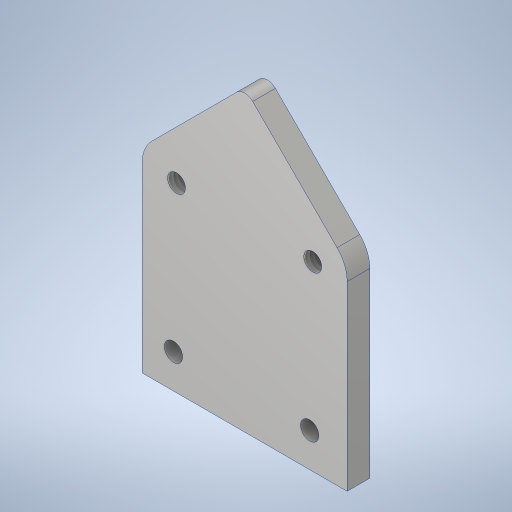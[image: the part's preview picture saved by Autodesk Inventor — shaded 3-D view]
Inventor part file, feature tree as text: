
AUTODESK INVENTOR PART (.ipt)
format: ipt  version: 2023.4 (Build 274418000, 418)  size: 270,848 bytes
history: native  units: in
note: dims shown in document units (in); Inventor stores cm internally (conversion verified against a paired STEP export)
features: sketch x2, hole x2, extrude x1
ambient origin geometry x8: Origin, YZ Plane, XZ Plane, XY Plane, X Axis, Y Axis, Z Axis, Center Point
bodies: Solid1 (feature_tree)
feature tree (5):
  sketch  "Sketch1"  dims[d0=0.257in d1=1.5in]
  extrude  "Extrusion1"  Depth=1.5in
  hole  "Hole1"  [1 undecoded]
  hole  "Hole2"  [1 undecoded]
  sketch  "Sketch2"  dims[d2=0.25in d3=0.25in d4=2.0in d5=0.125in d6=0.25in d7=0.0in d8=1.5in d9=0.375in d10=0.201in d11=0.75in d12=0.385in d13=0.25in d14=0.5635in d15=1.0in d16=0.8108in d17=0.196in d18=0.5in d19=0.385in d20=0.25in d21=0.5635in d22=1.0in d23=0.8108in]
note: 2 required parameter values undecoded (feature->parameter linkage not recoverable at this tier; creation-order binding heuristic only, values carry confidence <= 0.55)
